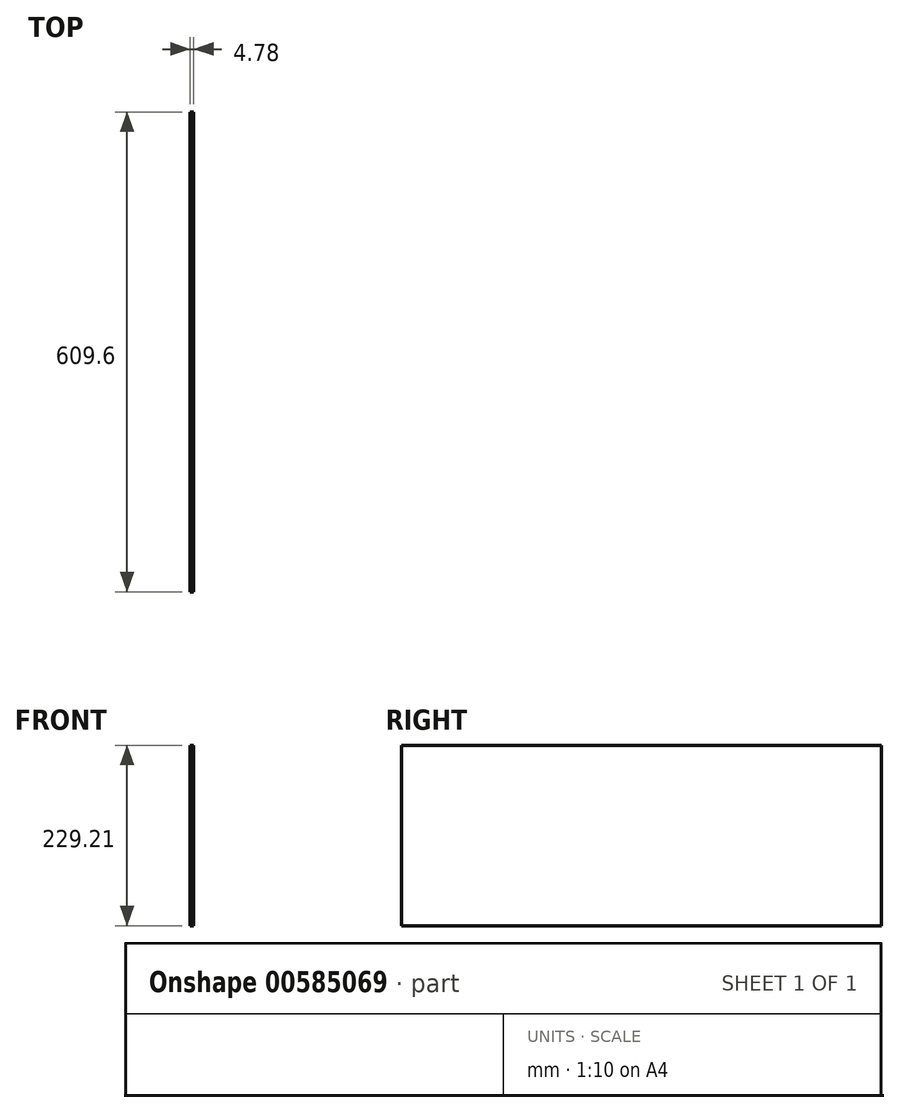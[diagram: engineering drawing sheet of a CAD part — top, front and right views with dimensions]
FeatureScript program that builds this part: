
annotation { "Feature Type Name" : "Feature", "Feature Type Description" : "" }
export const myFeature = defineFeature(function(context is Context, id is Id, definition is map)
    precondition{}
    {
        {
            var Q0;
            Q0=qCreatedBy(makeId("Right.planeOp"),FACE);
            var sketch = newSketch(context, id + "F0", { "sketchPlane" : qUnion([Q0])});
            skLineSegment(sketch, "E0.bottom", {"start": v(0, 0) * mm, "end": v(609.6, 0) * mm});
            skLineSegment(sketch, "E0.top", {"start": v(0, 229.2) * mm, "end": v(609.6, 229.2) * mm});
            skLineSegment(sketch, "E0.left", {"start": v(0, 0) * mm, "end": v(0, 229.2) * mm});
            skLineSegment(sketch, "E0.right", {"start": v(609.6, 0) * mm, "end": v(609.6, 229.2) * mm});
            skLineSegment(sketch, "E1.bottom", {"start": v(177.8, 229.2) * mm, "end": v(431.8, 229.2) * mm});
            skLineSegment(sketch, "E2.bottom", {"start": v(177.8, 178.4) * mm, "end": v(177.55, 178.4) * mm});
            skLineSegment(sketch, "E3.bottom", {"start": v(431.8, 178.4) * mm, "end": v(432.05, 178.4) * mm});
            skLineSegment(sketch, "E3.top", {"start": v(431.8, 229.2) * mm, "end": v(432.05, 229.2) * mm});
            skSolve(sketch);
        }
        {
            var Q0;
            Q0=makeQuery(id+"F0.imprint","IMPRINT",FACE,{"disambiguationData":[TD([[makeQuery(id+"F0.imprint","IMPRINT",EDGE,{"derivedFrom":sQuery(id+"F0.wireOp",EDGE,"E0.bottom")}),1.0]])]});
            extrude(context, id + "F1", {"entities" : qUnion([Q0]), "depth" : 4.78 * mm, "offsetDistance" : 25.4 * mm});
        }
    });
